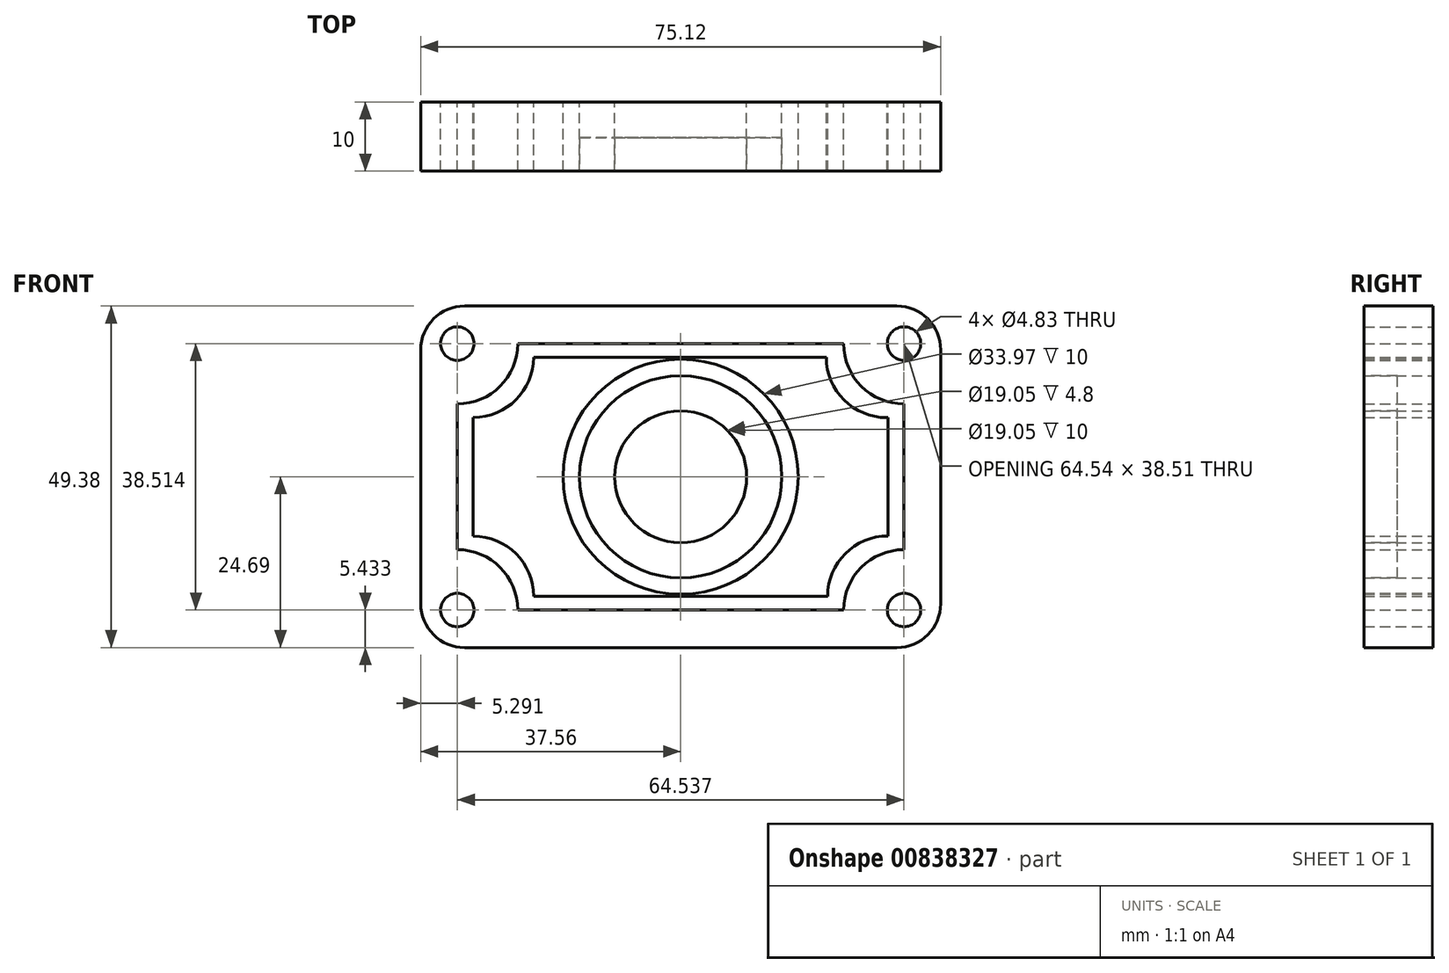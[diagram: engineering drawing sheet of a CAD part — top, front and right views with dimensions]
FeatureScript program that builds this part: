
annotation { "Feature Type Name" : "Feature", "Feature Type Description" : "" }
export const myFeature = defineFeature(function(context is Context, id is Id, definition is map)
    precondition{}
    {
        {
            var Q0;
            Q0=qCreatedBy(makeId("Front.planeOp"),FACE);
            var sketch = newSketch(context, id + "F0", { "sketchPlane" : qUnion([Q0])});
            skCircle(sketch, "E0", {"center": v(0, 0) * mm, "radius": 9.53 * mm});
            skCircle(sketch, "E1", {"center": v(0, 0) * mm, "radius": 14.6 * mm});
            skCircle(sketch, "E2", {"center": v(0, 0) * mm, "radius": 16.98 * mm});
            skLineSegment(sketch, "E3.bottom", {"start": v(21.23, -17.28) * mm, "end": v(-21.23, -17.28) * mm});
            skLineSegment(sketch, "E3.top", {"start": v(21.04, 17.28) * mm, "end": v(-21.25, 17.28) * mm});
            skLineSegment(sketch, "E3.left", {"start": v(29.96, -17.29) * mm, "end": v(29.96, -17.28) * mm});
            skLineSegment(sketch, "E3.right", {"start": v(-29.96, -8.57) * mm, "end": v(-29.96, 8.57) * mm});
            skLineSegment(sketch, "E4", {"start": v(21.04, 17.28) * mm, "end": v(21.04, 17.28) * mm});
            skLineSegment(sketch, "E5", {"start": v(29.77, 8.55) * mm, "end": v(29.96, 8.55) * mm});
            skLineSegment(sketch, "E6", {"start": v(21.23, -17.28) * mm, "end": v(21.23, -17.28) * mm});
            skLineSegment(sketch, "E7", {"start": v(29.96, -8.55) * mm, "end": v(29.96, -8.55) * mm});
            skPoint(sketch, "E8.visualSharp", {"position": v(21.23, -8.55) * mm});
            skArc(sketch, "E8.filletArc", {"start": v(29.96, -8.55) * mm, "mid": v(23.78, -11.1) * mm, "end": v(21.23, -17.28) * mm});
            skPoint(sketch, "E9.visualSharp", {"position": v(21.04, 8.55) * mm});
            skArc(sketch, "E9.filletArc", {"start": v(21.04, 17.28) * mm, "mid": v(23.6, 11.1) * mm, "end": v(29.77, 8.55) * mm});
            skLineSegment(sketch, "E10", {"start": v(-21.25, 17.28) * mm, "end": v(-21.25, 17.28) * mm});
            skLineSegment(sketch, "E11", {"start": v(-29.96, 8.57) * mm, "end": v(-29.96, 8.57) * mm});
            skPoint(sketch, "E12.visualSharp", {"position": v(-21.25, 8.57) * mm});
            skArc(sketch, "E12.filletArc", {"start": v(-29.96, 8.57) * mm, "mid": v(-23.8, 11.12) * mm, "end": v(-21.25, 17.28) * mm});
            skLineSegment(sketch, "E13", {"start": v(-29.96, -8.57) * mm, "end": v(-29.96, -8.57) * mm});
            skLineSegment(sketch, "E14", {"start": v(-21.23, -17.28) * mm, "end": v(-21.23, -17.3) * mm});
            skPoint(sketch, "E15.visualSharp", {"position": v(-21.23, -8.57) * mm});
            skArc(sketch, "E15.filletArc", {"start": v(-21.23, -17.3) * mm, "mid": v(-23.78, -11.13) * mm, "end": v(-29.96, -8.57) * mm});
            skLineSegment(sketch, "E16.bottom", {"start": v(23.54, -19.26) * mm, "end": v(-23.54, -19.26) * mm});
            skLineSegment(sketch, "E16.top", {"start": v(23.54, 19.26) * mm, "end": v(-23.54, 19.26) * mm});
            skLineSegment(sketch, "E16.left", {"start": v(32.27, -10.53) * mm, "end": v(32.27, 10.53) * mm});
            skLineSegment(sketch, "E16.right", {"start": v(-32.27, -10.53) * mm, "end": v(-32.27, 10.53) * mm});
            skLineSegment(sketch, "E17", {"start": v(29.89, -17.29) * mm, "end": v(29.96, -17.29) * mm});
            skArc(sketch, "E18", {"start": v(23.54, 19.26) * mm, "mid": v(26.1, 13.08) * mm, "end": v(32.27, 10.53) * mm});
            skPoint(sketch, "E19.orphan", {"position": v(29.96, 17.28) * mm});
            skArc(sketch, "E20", {"start": v(32.27, -10.53) * mm, "mid": v(26.1, -13.08) * mm, "end": v(23.54, -19.26) * mm});
            skArc(sketch, "E21", {"start": v(-23.54, -19.26) * mm, "mid": v(-26.1, -13.08) * mm, "end": v(-32.27, -10.53) * mm});
            skLineSegment(sketch, "E22.trimOffspring", {"start": v(29.96, -8.55) * mm, "end": v(29.96, 8.55) * mm});
            skPoint(sketch, "E23.orphan", {"position": v(-29.96, -17.28) * mm});
            skArc(sketch, "E24", {"start": v(-32.27, 10.53) * mm, "mid": v(-26.1, 13.08) * mm, "end": v(-23.54, 19.26) * mm});
            skCircle(sketch, "E25", {"center": v(-32.27, 19.26) * mm, "radius": 2.42 * mm});
            skCircle(sketch, "E26", {"center": v(-32.27, -19.26) * mm, "radius": 2.42 * mm});
            skCircle(sketch, "E27", {"center": v(32.27, 19.26) * mm, "radius": 2.42 * mm});
            skCircle(sketch, "E28", {"center": v(32.27, -19.26) * mm, "radius": 2.42 * mm});
            skLineSegment(sketch, "E29.bottom", {"start": v(-31.21, 24.69) * mm, "end": v(31.21, 24.69) * mm});
            skLineSegment(sketch, "E29.top", {"start": v(-31.21, -24.69) * mm, "end": v(31.21, -24.69) * mm});
            skLineSegment(sketch, "E29.left", {"start": v(-37.56, 18.34) * mm, "end": v(-37.56, -18.34) * mm});
            skLineSegment(sketch, "E29.right", {"start": v(37.56, 18.34) * mm, "end": v(37.56, -18.34) * mm});
            skPoint(sketch, "E30.visualSharp", {"position": v(-37.56, 24.69) * mm});
            skArc(sketch, "E30.filletArc", {"start": v(-31.21, 24.69) * mm, "mid": v(-35.7, 22.83) * mm, "end": v(-37.56, 18.34) * mm});
            skPoint(sketch, "E31.visualSharp", {"position": v(37.56, 24.69) * mm});
            skArc(sketch, "E31.filletArc", {"start": v(37.56, 18.34) * mm, "mid": v(35.7, 22.83) * mm, "end": v(31.21, 24.69) * mm});
            skPoint(sketch, "E32.visualSharp", {"position": v(37.56, -24.69) * mm});
            skArc(sketch, "E32.filletArc", {"start": v(31.21, -24.69) * mm, "mid": v(35.7, -22.83) * mm, "end": v(37.56, -18.34) * mm});
            skPoint(sketch, "E33.visualSharp", {"position": v(-37.56, -24.69) * mm});
            skArc(sketch, "E33.filletArc", {"start": v(-37.56, -18.34) * mm, "mid": v(-35.7, -22.83) * mm, "end": v(-31.21, -24.69) * mm});
            skSolve(sketch);
        }
        {
            var Q0;
            Q0=makeQuery(id+"F0.imprint","IMPRINT",FACE,{"disambiguationData":[TD([[makeQuery(id+"F0.imprint","IMPRINT",EDGE,{"derivedFrom":sQuery(id+"F0.wireOp",EDGE,"E2")}),-1.0]])]});
            var Q1;
            Q1=makeQuery(id+"F0.imprint","IMPRINT",FACE,{"disambiguationData":[TD([[makeQuery(id+"F0.imprint","IMPRINT",EDGE,{"derivedFrom":sQuery(id+"F0.wireOp",EDGE,"E0")}),-1.0]])]});
            extrude(context, id + "F1", {"entities" : qUnion([Q0, Q1]), "depth" : 10 * mm, "offsetDistance" : 25 * mm});
        }
        {
            var Q0;
            Q0=makeQuery(id+"F1.opExtrude","CAP_FACE",FACE,{"disambiguationData":[OSD([sQuery(id+"F0.wireOp",EDGE,"E0"),sQuery(id+"F0.wireOp",EDGE,"E1")])],"isStart":false});
            extrude(context, id + "F2", {"entities" : qUnion([Q0]), "oppositeDirection" : true, "depth" : 4.8 * mm, "offsetDistance" : 25 * mm});
        }
        {
            var Q0;
            Q0=makeQuery(id+"F0.imprint","IMPRINT",FACE,{"disambiguationData":[TD([[makeQuery(id+"F0.imprint","IMPRINT",EDGE,{"derivedFrom":sQuery(id+"F0.wireOp",EDGE,"E16.bottom")}),1.0]])]});
            extrude(context, id + "F3", {"entities" : qUnion([Q0]), "depth" : 10 * mm, "offsetDistance" : 25 * mm});
        }
    });
